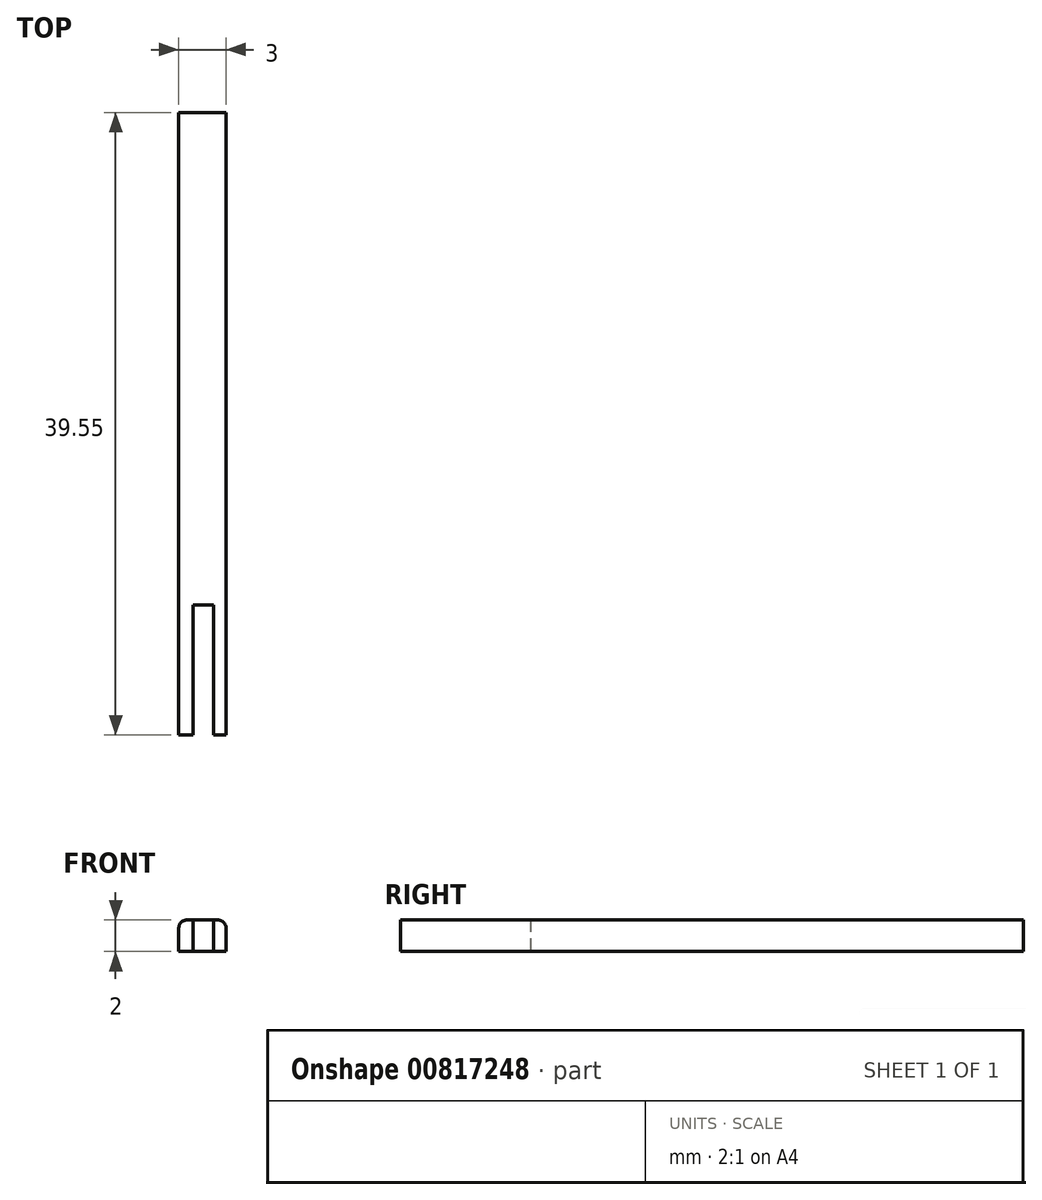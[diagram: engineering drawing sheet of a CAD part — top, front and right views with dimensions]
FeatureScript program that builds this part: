
annotation { "Feature Type Name" : "Feature", "Feature Type Description" : "" }
export const myFeature = defineFeature(function(context is Context, id is Id, definition is map)
    precondition{}
    {
        {
            var Q0;
            Q0=qCreatedBy(makeId("Top.planeOp"),FACE);
            var sketch = newSketch(context, id + "F0", { "sketchPlane" : qUnion([Q0])});
            skLineSegment(sketch, "E0.top", {"start": v(7, 48.8) * mm, "end": v(4, 48.8) * mm});
            skLineSegment(sketch, "E0.left", {"start": v(7, 9.25) * mm, "end": v(7, 48.8) * mm});
            skLineSegment(sketch, "E0.right", {"start": v(4, 9.25) * mm, "end": v(4, 48.8) * mm});
            skPoint(sketch, "E0.middle", {"position": v(5.5, 29.02) * mm});
            skLineSegment(sketch, "E1.top", {"start": v(6.2, 17.5) * mm, "end": v(4.9, 17.5) * mm});
            skLineSegment(sketch, "E1.left", {"start": v(6.2, 9.25) * mm, "end": v(6.2, 17.5) * mm});
            skLineSegment(sketch, "E1.right", {"start": v(4.9, 9.25) * mm, "end": v(4.9, 17.5) * mm});
            skLineSegment(sketch, "E2.trimOffspring", {"start": v(4.9, 9.25) * mm, "end": v(4, 9.25) * mm});
            skLineSegment(sketch, "E3", {"start": v(6.2, 9.25) * mm, "end": v(7, 9.25) * mm});
            skSolve(sketch);
        }
        {
            var Q0;
            Q0=makeQuery(id+"F0.imprint","IMPRINT",FACE,{"disambiguationData":[TD([[makeQuery(id+"F0.imprint","IMPRINT",EDGE,{"derivedFrom":sQuery(id+"F0.wireOp",EDGE,"E0.top")}),1.0]])]});
            extrude(context, id + "F1", {"entities" : qUnion([Q0]), "depth" : 1 * mm, "offsetDistance" : 25 * mm, "hasSecondDirection" : true, "secondDirectionOppositeDirection" : true, "secondDirectionDepth" : 1 * mm});
        }
        {
            var Q0;
            Q0=makeQuery(id+"F1.opExtrude","CAP_EDGE",EDGE,{"disambiguationData":[OSD([sQuery(id+"F0.wireOp",EDGE,"E0.right")])],"isStart":false});
            var Q1;
            Q1=makeQuery(id+"F1.opExtrude","CAP_EDGE",EDGE,{"disambiguationData":[OSD([sQuery(id+"F0.wireOp",EDGE,"E0.left")])],"isStart":false});
            fillet(context, id + "F2", {"entities" : qUnion([Q0, Q1]), "radius" : .5 * mm, "tangentPropagation" : true, "allowEdgeOverflow" : false});
        }
    });
